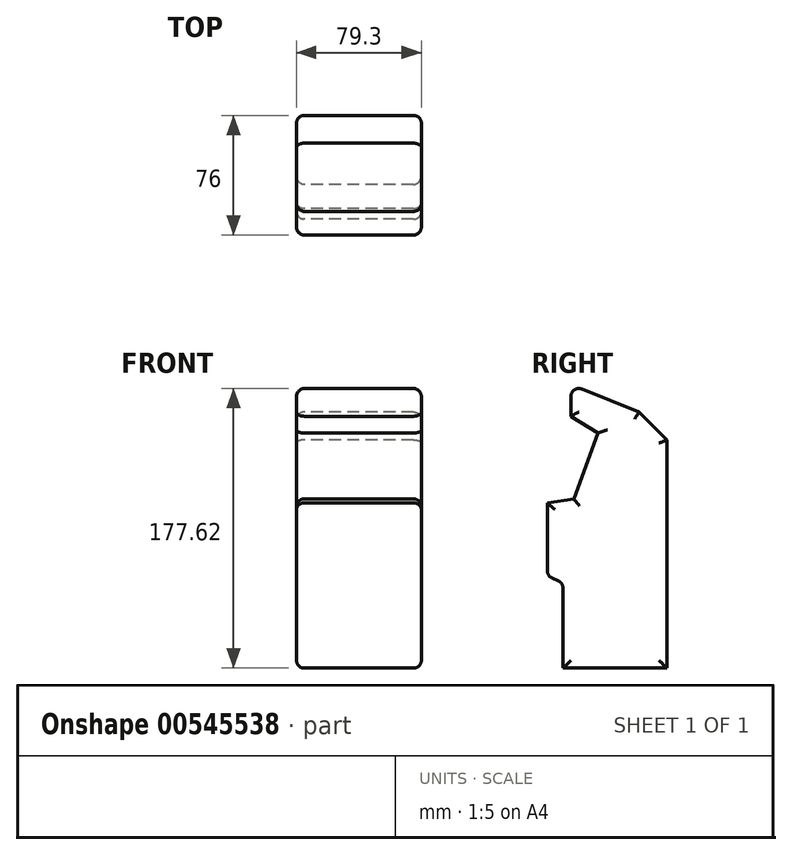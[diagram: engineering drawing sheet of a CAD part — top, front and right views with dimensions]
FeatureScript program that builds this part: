
annotation { "Feature Type Name" : "Feature", "Feature Type Description" : "" }
export const myFeature = defineFeature(function(context is Context, id is Id, definition is map)
    precondition{}
    {
        {
            var Q0;
            Q0=qCreatedBy(makeId("Right.planeOp"),FACE);
            var sketch = newSketch(context, id + "F0", { "sketchPlane" : qUnion([Q0])});
            skLineSegment(sketch, "E0", {"start": v(0, 0) * mm, "end": v(0, 145) * mm});
            skLineSegment(sketch, "E1", {"start": v(0, 145) * mm, "end": v(-17.68, 162.68) * mm});
            skLineSegment(sketch, "E2", {"start": v(-17.68, 162.68) * mm, "end": v(-61, 180) * mm});
            skLineSegment(sketch, "E3", {"start": v(-61, 180) * mm, "end": v(-61, 160) * mm});
            skLineSegment(sketch, "E4", {"start": v(-61, 160) * mm, "end": v(-43.96, 149.32) * mm});
            skLineSegment(sketch, "E5", {"start": v(-43.96, 149.32) * mm, "end": v(-59.18, 107.5) * mm});
            skLineSegment(sketch, "E6", {"start": v(-59.18, 107.5) * mm, "end": v(-76, 105) * mm});
            skLineSegment(sketch, "E7", {"start": v(-76, 105) * mm, "end": v(-76, 58.58) * mm});
            skLineSegment(sketch, "E8", {"start": v(-76, 58.58) * mm, "end": v(-66, 54) * mm});
            skLineSegment(sketch, "E9", {"start": v(-66, 54) * mm, "end": v(-66, 0) * mm});
            skLineSegment(sketch, "E10", {"start": v(-66, 0) * mm, "end": v(0, 0) * mm});
            skSolve(sketch);
        }
        {
            var Q0;
            Q0=makeQuery(id+"F0.imprint","IMPRINT",FACE,{"disambiguationData":[TD([[makeQuery(id+"F0.imprint","IMPRINT",EDGE,{"derivedFrom":sQuery(id+"F0.wireOp",EDGE,"E0")}),1.0]])]});
            extrude(context, id + "F1", {"entities" : qUnion([Q0]), "endBound" : BoundingType.SYMMETRIC, "depth" : 79.3 * mm, "offsetDistance" : 25 * mm});
        }
        {
            var Q0;
            Q0=makeQuery(id+"F1.opExtrude","SWEPT_EDGE",EDGE,{"disambiguationData":[OSD([sQuery(id+"F0.wireOp",EDGE,"E7"),sQuery(id+"F0.wireOp",EDGE,"E8")])]});
            var Q1;
            Q1=makeQuery(id+"F1.opExtrude","SWEPT_EDGE",EDGE,{"disambiguationData":[OSD([sQuery(id+"F0.wireOp",EDGE,"E8"),sQuery(id+"F0.wireOp",EDGE,"E9")])]});
            var Q2;
            Q2=makeQuery(id+"F1.opExtrude","CAP_EDGE",EDGE,{"disambiguationData":[OSD([sQuery(id+"F0.wireOp",EDGE,"E9")])],"isStart":true});
            var Q3;
            Q3=makeQuery(id+"F1.opExtrude","CAP_EDGE",EDGE,{"disambiguationData":[OSD([sQuery(id+"F0.wireOp",EDGE,"E7")])],"isStart":true});
            var Q4;
            Q4=makeQuery(id+"F1.opExtrude","CAP_EDGE",EDGE,{"disambiguationData":[OSD([sQuery(id+"F0.wireOp",EDGE,"E6")])],"isStart":true});
            var Q5;
            Q5=makeQuery(id+"F1.opExtrude","CAP_EDGE",EDGE,{"disambiguationData":[OSD([sQuery(id+"F0.wireOp",EDGE,"E5")])],"isStart":true});
            var Q6;
            Q6=makeQuery(id+"F1.opExtrude","CAP_FACE",FACE,{"disambiguationData":[OSD([sQuery(id+"F0.wireOp",EDGE,"E0"),sQuery(id+"F0.wireOp",EDGE,"E1"),sQuery(id+"F0.wireOp",EDGE,"E2"),sQuery(id+"F0.wireOp",EDGE,"E3"),sQuery(id+"F0.wireOp",EDGE,"E4"),sQuery(id+"F0.wireOp",EDGE,"E5"),sQuery(id+"F0.wireOp",EDGE,"E6"),sQuery(id+"F0.wireOp",EDGE,"E7"),sQuery(id+"F0.wireOp",EDGE,"E8"),sQuery(id+"F0.wireOp",EDGE,"E9"),sQuery(id+"F0.wireOp",EDGE,"E10")])],"isStart":true});
            var Q7;
            Q7=makeQuery(id+"F1.opExtrude","CAP_FACE",FACE,{"disambiguationData":[OSD([sQuery(id+"F0.wireOp",EDGE,"E0"),sQuery(id+"F0.wireOp",EDGE,"E1"),sQuery(id+"F0.wireOp",EDGE,"E2"),sQuery(id+"F0.wireOp",EDGE,"E3"),sQuery(id+"F0.wireOp",EDGE,"E4"),sQuery(id+"F0.wireOp",EDGE,"E5"),sQuery(id+"F0.wireOp",EDGE,"E6"),sQuery(id+"F0.wireOp",EDGE,"E7"),sQuery(id+"F0.wireOp",EDGE,"E8"),sQuery(id+"F0.wireOp",EDGE,"E9"),sQuery(id+"F0.wireOp",EDGE,"E10")])],"isStart":false});
            var Q8;
            Q8=makeQuery(id+"F1.opExtrude","SWEPT_EDGE",EDGE,{"disambiguationData":[OSD([sQuery(id+"F0.wireOp",EDGE,"E2"),sQuery(id+"F0.wireOp",EDGE,"E3")])]});
            fillet(context, id + "F2", {"entities" : qUnion([Q0, Q1, Q2, Q3, Q4, Q5, Q6, Q7, Q8]), "radius" : 5 * mm, "tangentPropagation" : true, "allowEdgeOverflow" : false});
        }
    });
